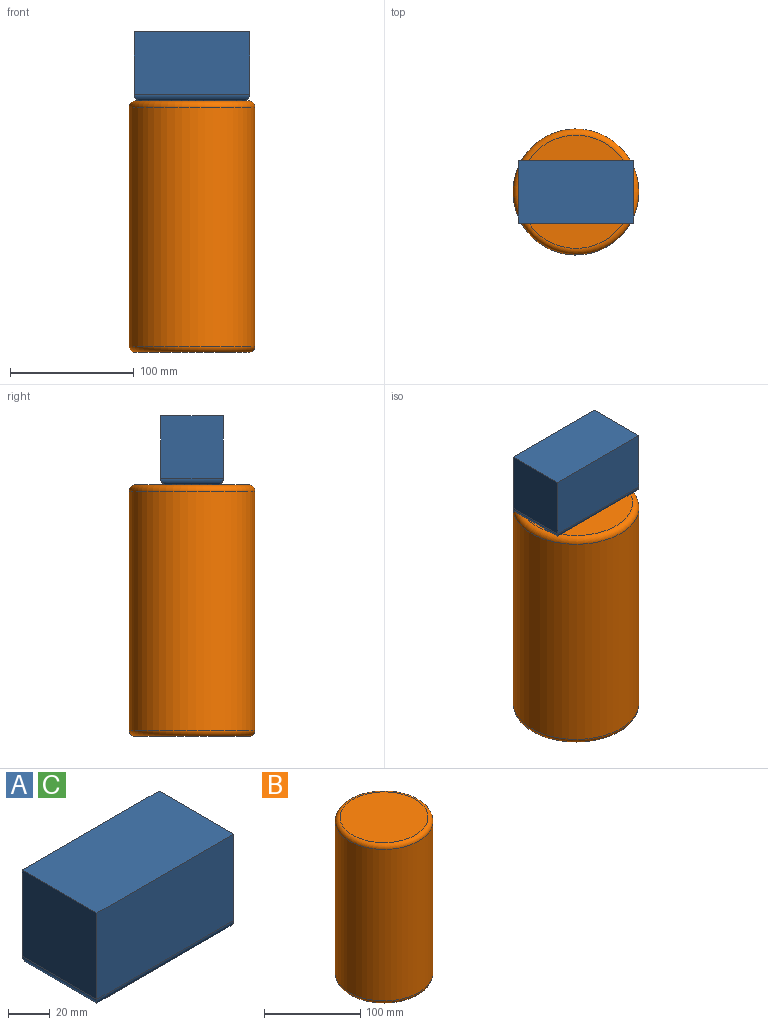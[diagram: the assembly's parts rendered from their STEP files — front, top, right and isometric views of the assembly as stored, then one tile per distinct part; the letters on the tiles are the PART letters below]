
ASSEMBLY  parts=3 mates=1
PART A: 10 faces, bbox 93x50.8x55.9 mm
  f0: plane 93.02x50.8mm, normal (0,0,1), area 4725.3mm2, adj f1,f3,f4,f5
  f1: plane 50.81x50.8mm, normal (-1,0,0), area 2581.4mm2, adj f0,f4,f5,f9
  f2: plane 82.86x40.64mm, normal (0,0,-1), area 3367.3mm2, adj f6,f7,f8,f9
  f3: plane 50.81x50.8mm, normal (1,0,0), area 2581.4mm2, adj f0,f4,f5,f6
  f4: plane 93.02x50.81mm, normal (0,-1,0), area 4726.6mm2, adj f0,f1,f3,f7
  f5: plane 93.02x50.81mm, normal (0,1,0), area 4726.6mm2, adj f0,f1,f3,f8
  f6: cylinder r=5.08mm len=50.8mm, axis (0,1,0), area 375.9mm2, adj f2,f3,f7,f8
  f7: cylinder r=5.08mm len=93.02mm, axis (-1,0,0), area 712.8mm2, adj f2,f4,f6,f9
  f8: cylinder r=5.08mm len=93.02mm, axis (1,0,0), area 712.8mm2, adj f2,f5,f6,f9
  f9: cylinder r=5.08mm len=50.8mm, axis (0,-1,0), area 375.9mm2, adj f1,f2,f7,f8
PART B: 5 faces, bbox 110x110x203.2 mm
  f0: cylinder r=50.8mm len=193.04mm, axis (0,0,-1), area 61615.6mm2, adj f3,f4
  f1: plane 91.44x91.44mm, normal (0,0,1), area 6566.9mm2, adj f4
  f2: plane 91.44x91.44mm, normal (0,0,-1), area 6566.9mm2, adj f3
  f3: torus R=45.72mm, axis (0,0,1), area 2454.4mm2, adj f0,f2
  f4: torus R=45.72mm, axis (0,0,1), area 2454.4mm2, adj f0,f1
PART C: same geometry as A
PLACE A t=(-179.23,19.73,-0.4)mm fixed
PLACE B t=(-177.79,-5.67,-231.15)mm
PLACE C t=(-179.23,19.73,-0.4)mm
MATE planar A.f2 <-> B.f0  axis (0,0,-1) through (-177.79,-5.67,-27.95)mm
